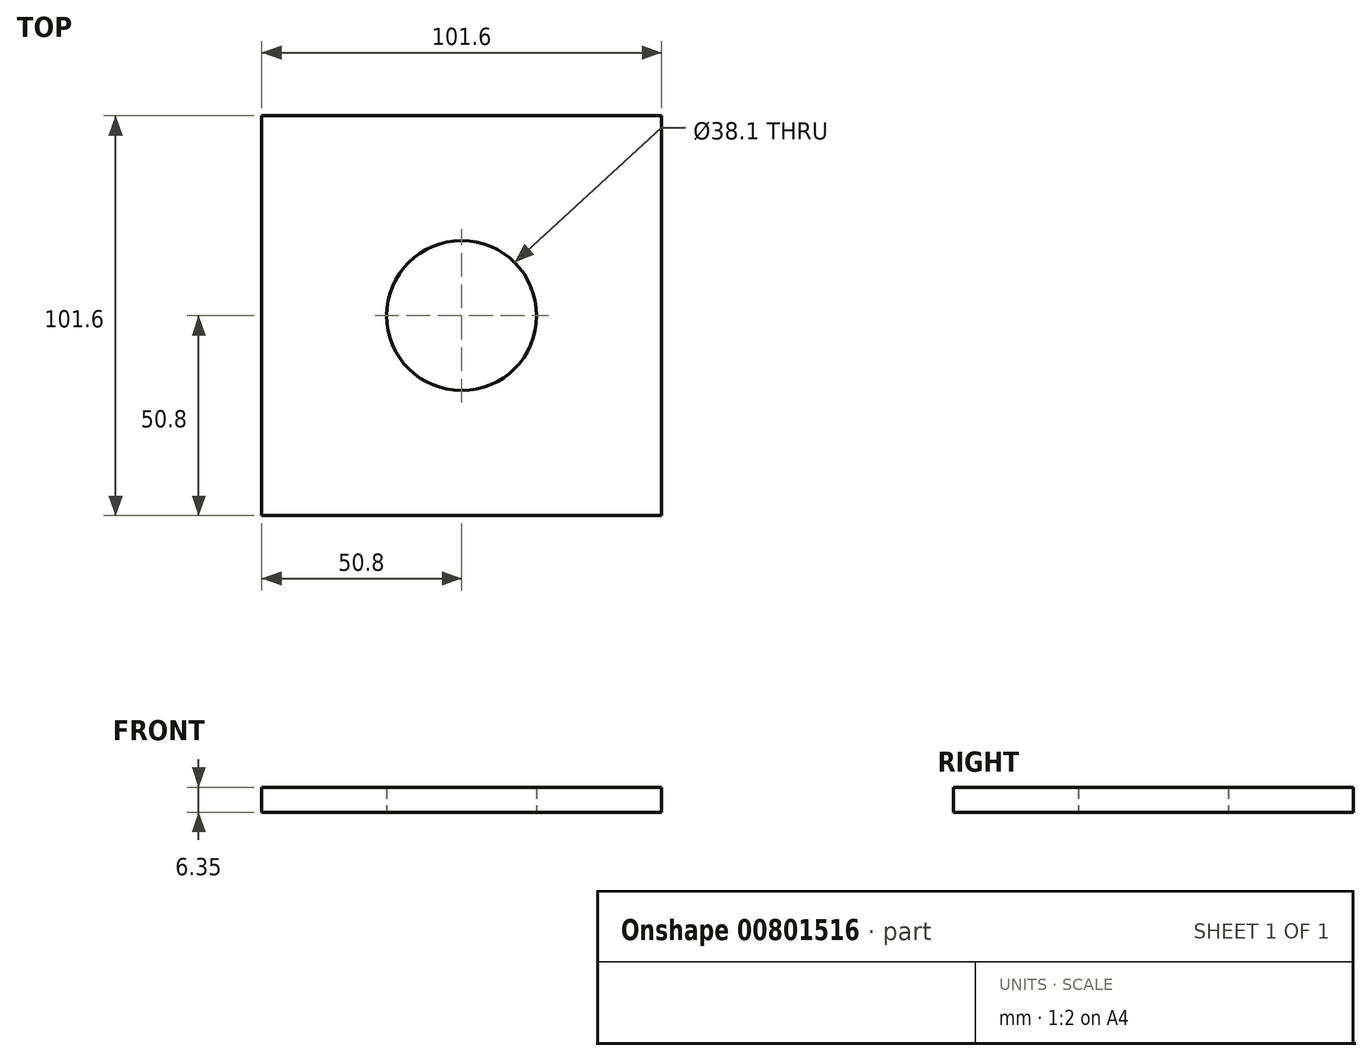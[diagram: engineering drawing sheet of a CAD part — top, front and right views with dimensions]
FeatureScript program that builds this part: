
annotation { "Feature Type Name" : "Feature", "Feature Type Description" : "" }
export const myFeature = defineFeature(function(context is Context, id is Id, definition is map)
    precondition{}
    {
        {
            var Q0;
            Q0=qCreatedBy(makeId("Top.planeOp"),FACE);
            var sketch = newSketch(context, id + "F0", { "sketchPlane" : qUnion([Q0])});
            skLineSegment(sketch, "E0.bottom", {"start": v(-50.8, 50.8) * mm, "end": v(50.8, 50.8) * mm});
            skLineSegment(sketch, "E0.top", {"start": v(-50.8, -50.8) * mm, "end": v(50.8, -50.8) * mm});
            skLineSegment(sketch, "E0.left", {"start": v(-50.8, 50.8) * mm, "end": v(-50.8, -50.8) * mm});
            skLineSegment(sketch, "E0.right", {"start": v(50.8, 50.8) * mm, "end": v(50.8, -50.8) * mm});
            skCircle(sketch, "E1", {"center": v(0, 0) * mm, "radius": 19.05 * mm});
            skSolve(sketch);
        }
        {
            var Q0;
            Q0 = qSketchRegion(id + "F0", true);
            extrude(context, id + "F1", {"entities" : qUnion([Q0]), "depth" : 6.35 * mm, "offsetDistance" : 25.4 * mm});
        }
    });
